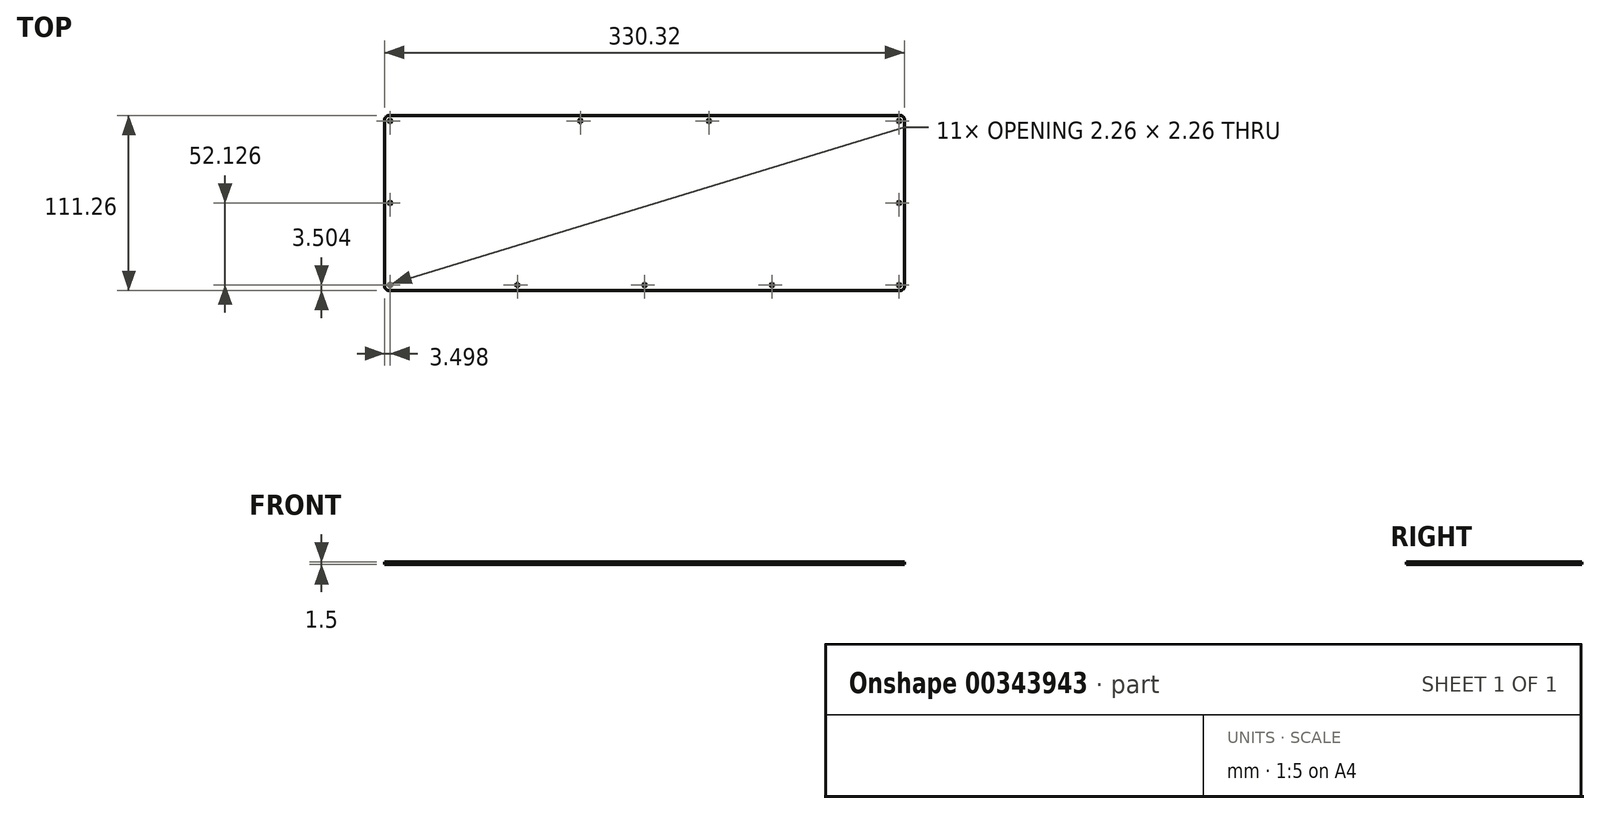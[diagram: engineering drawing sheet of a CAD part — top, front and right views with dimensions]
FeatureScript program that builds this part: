
annotation { "Feature Type Name" : "Feature", "Feature Type Description" : "" }
export const myFeature = defineFeature(function(context is Context, id is Id, definition is map)
    precondition{}
    {
        {
            var Q0;
            Q0=qCreatedBy(makeId("Top.planeOp"),FACE);
            var sketch = newSketch(context, id + "F0", { "sketchPlane" : qUnion([Q0])});
            skLineSegment(sketch, "E0", {"start": v(162.16, 55.62) * mm, "end": v(162.4, 55.62) * mm});
            skLineSegment(sketch, "E1", {"start": v(162.4, 55.62) * mm, "end": v(162.63, 55.59) * mm});
            skLineSegment(sketch, "E2", {"start": v(162.63, 55.59) * mm, "end": v(162.86, 55.54) * mm});
            skLineSegment(sketch, "E3", {"start": v(162.86, 55.54) * mm, "end": v(163.1, 55.48) * mm});
            skLineSegment(sketch, "E4", {"start": v(163.1, 55.48) * mm, "end": v(163.31, 55.4) * mm});
            skLineSegment(sketch, "E5", {"start": v(163.31, 55.4) * mm, "end": v(163.53, 55.3) * mm});
            skLineSegment(sketch, "E6", {"start": v(163.53, 55.3) * mm, "end": v(163.73, 55.18) * mm});
            skLineSegment(sketch, "E7", {"start": v(163.73, 55.18) * mm, "end": v(163.93, 55.05) * mm});
            skLineSegment(sketch, "E8", {"start": v(163.93, 55.05) * mm, "end": v(164.11, 54.9) * mm});
            skLineSegment(sketch, "E9", {"start": v(164.11, 54.9) * mm, "end": v(164.29, 54.75) * mm});
            skLineSegment(sketch, "E10", {"start": v(164.29, 54.75) * mm, "end": v(164.45, 54.57) * mm});
            skLineSegment(sketch, "E11", {"start": v(164.45, 54.57) * mm, "end": v(164.6, 54.39) * mm});
            skLineSegment(sketch, "E12", {"start": v(164.6, 54.39) * mm, "end": v(164.72, 54.2) * mm});
            skLineSegment(sketch, "E13", {"start": v(164.72, 54.2) * mm, "end": v(164.84, 53.99) * mm});
            skLineSegment(sketch, "E14", {"start": v(164.84, 53.99) * mm, "end": v(164.93, 53.77) * mm});
            skLineSegment(sketch, "E15", {"start": v(164.93, 53.77) * mm, "end": v(165.02, 53.55) * mm});
            skLineSegment(sketch, "E16", {"start": v(165.02, 53.55) * mm, "end": v(165.08, 53.33) * mm});
            skLineSegment(sketch, "E17", {"start": v(165.08, 53.33) * mm, "end": v(165.13, 53.1) * mm});
            skLineSegment(sketch, "E18", {"start": v(165.13, 53.1) * mm, "end": v(165.15, 52.86) * mm});
            skLineSegment(sketch, "E19", {"start": v(165.15, 52.86) * mm, "end": v(165.16, 52.62) * mm});
            skLineSegment(sketch, "E20", {"start": v(165.16, 52.62) * mm, "end": v(165.16, -52.63) * mm});
            skLineSegment(sketch, "E21", {"start": v(165.16, -52.63) * mm, "end": v(165.15, -52.86) * mm});
            skLineSegment(sketch, "E22", {"start": v(165.15, -52.86) * mm, "end": v(165.13, -53.1) * mm});
            skLineSegment(sketch, "E23", {"start": v(165.13, -53.1) * mm, "end": v(165.08, -53.33) * mm});
            skLineSegment(sketch, "E24", {"start": v(165.08, -53.33) * mm, "end": v(165.02, -53.55) * mm});
            skLineSegment(sketch, "E25", {"start": v(165.02, -53.55) * mm, "end": v(164.93, -53.77) * mm});
            skLineSegment(sketch, "E26", {"start": v(164.93, -53.77) * mm, "end": v(164.84, -53.99) * mm});
            skLineSegment(sketch, "E27", {"start": v(164.84, -53.99) * mm, "end": v(164.72, -54.2) * mm});
            skLineSegment(sketch, "E28", {"start": v(164.72, -54.2) * mm, "end": v(164.6, -54.39) * mm});
            skLineSegment(sketch, "E29", {"start": v(164.6, -54.39) * mm, "end": v(164.45, -54.57) * mm});
            skLineSegment(sketch, "E30", {"start": v(164.45, -54.57) * mm, "end": v(164.29, -54.75) * mm});
            skLineSegment(sketch, "E31", {"start": v(164.29, -54.75) * mm, "end": v(164.11, -54.9) * mm});
            skLineSegment(sketch, "E32", {"start": v(164.11, -54.9) * mm, "end": v(163.93, -55.05) * mm});
            skLineSegment(sketch, "E33", {"start": v(163.93, -55.05) * mm, "end": v(163.73, -55.18) * mm});
            skLineSegment(sketch, "E34", {"start": v(163.73, -55.18) * mm, "end": v(163.53, -55.3) * mm});
            skLineSegment(sketch, "E35", {"start": v(163.53, -55.3) * mm, "end": v(163.31, -55.4) * mm});
            skLineSegment(sketch, "E36", {"start": v(163.31, -55.4) * mm, "end": v(163.1, -55.48) * mm});
            skLineSegment(sketch, "E37", {"start": v(163.1, -55.48) * mm, "end": v(162.86, -55.54) * mm});
            skLineSegment(sketch, "E38", {"start": v(162.86, -55.54) * mm, "end": v(162.63, -55.59) * mm});
            skLineSegment(sketch, "E39", {"start": v(162.63, -55.59) * mm, "end": v(162.4, -55.62) * mm});
            skLineSegment(sketch, "E40", {"start": v(162.4, -55.62) * mm, "end": v(162.16, -55.63) * mm});
            skLineSegment(sketch, "E41", {"start": v(162.16, -55.63) * mm, "end": v(-162.16, -55.63) * mm});
            skLineSegment(sketch, "E42", {"start": v(-162.16, -55.63) * mm, "end": v(-162.4, -55.62) * mm});
            skLineSegment(sketch, "E43", {"start": v(-162.4, -55.62) * mm, "end": v(-162.63, -55.59) * mm});
            skLineSegment(sketch, "E44", {"start": v(-162.63, -55.59) * mm, "end": v(-162.86, -55.54) * mm});
            skLineSegment(sketch, "E45", {"start": v(-162.86, -55.54) * mm, "end": v(-163.09, -55.48) * mm});
            skLineSegment(sketch, "E46", {"start": v(-163.09, -55.48) * mm, "end": v(-163.31, -55.4) * mm});
            skLineSegment(sketch, "E47", {"start": v(-163.31, -55.4) * mm, "end": v(-163.52, -55.3) * mm});
            skLineSegment(sketch, "E48", {"start": v(-163.52, -55.3) * mm, "end": v(-163.73, -55.18) * mm});
            skLineSegment(sketch, "E49", {"start": v(-163.73, -55.18) * mm, "end": v(-163.93, -55.05) * mm});
            skLineSegment(sketch, "E50", {"start": v(-163.93, -55.05) * mm, "end": v(-164.11, -54.9) * mm});
            skLineSegment(sketch, "E51", {"start": v(-164.11, -54.9) * mm, "end": v(-164.28, -54.75) * mm});
            skLineSegment(sketch, "E52", {"start": v(-164.28, -54.75) * mm, "end": v(-164.44, -54.57) * mm});
            skLineSegment(sketch, "E53", {"start": v(-164.44, -54.57) * mm, "end": v(-164.6, -54.39) * mm});
            skLineSegment(sketch, "E54", {"start": v(-164.6, -54.39) * mm, "end": v(-164.72, -54.2) * mm});
            skLineSegment(sketch, "E55", {"start": v(-164.72, -54.2) * mm, "end": v(-164.84, -53.99) * mm});
            skLineSegment(sketch, "E56", {"start": v(-164.84, -53.99) * mm, "end": v(-164.93, -53.77) * mm});
            skLineSegment(sketch, "E57", {"start": v(-164.93, -53.77) * mm, "end": v(-165.02, -53.55) * mm});
            skLineSegment(sketch, "E58", {"start": v(-165.02, -53.55) * mm, "end": v(-165.08, -53.33) * mm});
            skLineSegment(sketch, "E59", {"start": v(-165.08, -53.33) * mm, "end": v(-165.13, -53.1) * mm});
            skLineSegment(sketch, "E60", {"start": v(-165.13, -53.1) * mm, "end": v(-165.15, -52.86) * mm});
            skLineSegment(sketch, "E61", {"start": v(-165.15, -52.86) * mm, "end": v(-165.16, -52.63) * mm});
            skLineSegment(sketch, "E62", {"start": v(-165.16, -52.63) * mm, "end": v(-165.16, 52.62) * mm});
            skLineSegment(sketch, "E63", {"start": v(-165.16, 52.62) * mm, "end": v(-165.15, 52.86) * mm});
            skLineSegment(sketch, "E64", {"start": v(-165.15, 52.86) * mm, "end": v(-165.13, 53.1) * mm});
            skLineSegment(sketch, "E65", {"start": v(-165.13, 53.1) * mm, "end": v(-165.08, 53.33) * mm});
            skLineSegment(sketch, "E66", {"start": v(-165.08, 53.33) * mm, "end": v(-165.02, 53.55) * mm});
            skLineSegment(sketch, "E67", {"start": v(-165.02, 53.55) * mm, "end": v(-164.93, 53.77) * mm});
            skLineSegment(sketch, "E68", {"start": v(-164.93, 53.77) * mm, "end": v(-164.84, 53.99) * mm});
            skLineSegment(sketch, "E69", {"start": v(-164.84, 53.99) * mm, "end": v(-164.72, 54.2) * mm});
            skLineSegment(sketch, "E70", {"start": v(-164.72, 54.2) * mm, "end": v(-164.6, 54.39) * mm});
            skLineSegment(sketch, "E71", {"start": v(-164.6, 54.39) * mm, "end": v(-164.44, 54.57) * mm});
            skLineSegment(sketch, "E72", {"start": v(-164.44, 54.57) * mm, "end": v(-164.28, 54.75) * mm});
            skLineSegment(sketch, "E73", {"start": v(-164.28, 54.75) * mm, "end": v(-164.11, 54.9) * mm});
            skLineSegment(sketch, "E74", {"start": v(-164.11, 54.9) * mm, "end": v(-163.93, 55.05) * mm});
            skLineSegment(sketch, "E75", {"start": v(-163.93, 55.05) * mm, "end": v(-163.73, 55.18) * mm});
            skLineSegment(sketch, "E76", {"start": v(-163.73, 55.18) * mm, "end": v(-163.52, 55.3) * mm});
            skLineSegment(sketch, "E77", {"start": v(-163.52, 55.3) * mm, "end": v(-163.31, 55.4) * mm});
            skLineSegment(sketch, "E78", {"start": v(-163.31, 55.4) * mm, "end": v(-163.09, 55.48) * mm});
            skLineSegment(sketch, "E79", {"start": v(-163.09, 55.48) * mm, "end": v(-162.86, 55.54) * mm});
            skLineSegment(sketch, "E80", {"start": v(-162.86, 55.54) * mm, "end": v(-162.63, 55.59) * mm});
            skLineSegment(sketch, "E81", {"start": v(-162.63, 55.59) * mm, "end": v(-162.4, 55.62) * mm});
            skLineSegment(sketch, "E82", {"start": v(-162.4, 55.62) * mm, "end": v(-162.16, 55.63) * mm});
            skLineSegment(sketch, "E83", {"start": v(-162.16, 55.63) * mm, "end": v(162.16, 55.62) * mm});
            skLineSegment(sketch, "E84", {"start": v(161.31, -51.05) * mm, "end": v(161, -51.21) * mm});
            skLineSegment(sketch, "E85", {"start": v(161, -51.21) * mm, "end": v(160.75, -51.46) * mm});
            skLineSegment(sketch, "E86", {"start": v(160.75, -51.46) * mm, "end": v(160.59, -51.78) * mm});
            skLineSegment(sketch, "E87", {"start": v(160.59, -51.78) * mm, "end": v(160.53, -52.13) * mm});
            skLineSegment(sketch, "E88", {"start": v(160.53, -52.13) * mm, "end": v(160.59, -52.48) * mm});
            skLineSegment(sketch, "E89", {"start": v(160.59, -52.48) * mm, "end": v(160.75, -52.79) * mm});
            skLineSegment(sketch, "E90", {"start": v(160.75, -52.79) * mm, "end": v(161, -53.04) * mm});
            skLineSegment(sketch, "E91", {"start": v(161, -53.04) * mm, "end": v(161.31, -53.2) * mm});
            skLineSegment(sketch, "E92", {"start": v(161.31, -53.2) * mm, "end": v(161.66, -53.26) * mm});
            skLineSegment(sketch, "E93", {"start": v(161.66, -53.26) * mm, "end": v(162.01, -53.2) * mm});
            skLineSegment(sketch, "E94", {"start": v(162.01, -53.2) * mm, "end": v(162.33, -53.04) * mm});
            skLineSegment(sketch, "E95", {"start": v(162.33, -53.04) * mm, "end": v(162.58, -52.79) * mm});
            skLineSegment(sketch, "E96", {"start": v(162.58, -52.79) * mm, "end": v(162.74, -52.48) * mm});
            skLineSegment(sketch, "E97", {"start": v(162.74, -52.48) * mm, "end": v(162.8, -52.13) * mm});
            skLineSegment(sketch, "E98", {"start": v(162.8, -52.13) * mm, "end": v(162.74, -51.78) * mm});
            skLineSegment(sketch, "E99", {"start": v(162.74, -51.78) * mm, "end": v(162.58, -51.46) * mm});
            skLineSegment(sketch, "E100", {"start": v(162.58, -51.46) * mm, "end": v(162.33, -51.21) * mm});
            skLineSegment(sketch, "E101", {"start": v(162.33, -51.21) * mm, "end": v(162.01, -51.05) * mm});
            skLineSegment(sketch, "E102", {"start": v(162.01, -51.05) * mm, "end": v(161.66, -51) * mm});
            skLineSegment(sketch, "E103", {"start": v(161.66, -51) * mm, "end": v(161.31, -51.05) * mm});
            skLineSegment(sketch, "E104", {"start": v(80.48, -51.05) * mm, "end": v(80.17, -51.21) * mm});
            skLineSegment(sketch, "E105", {"start": v(80.17, -51.21) * mm, "end": v(79.92, -51.46) * mm});
            skLineSegment(sketch, "E106", {"start": v(79.92, -51.46) * mm, "end": v(79.76, -51.78) * mm});
            skLineSegment(sketch, "E107", {"start": v(79.76, -51.78) * mm, "end": v(79.7, -52.13) * mm});
            skLineSegment(sketch, "E108", {"start": v(79.7, -52.13) * mm, "end": v(79.76, -52.48) * mm});
            skLineSegment(sketch, "E109", {"start": v(79.76, -52.48) * mm, "end": v(79.92, -52.79) * mm});
            skLineSegment(sketch, "E110", {"start": v(79.92, -52.79) * mm, "end": v(80.17, -53.04) * mm});
            skLineSegment(sketch, "E111", {"start": v(80.17, -53.04) * mm, "end": v(80.48, -53.2) * mm});
            skLineSegment(sketch, "E112", {"start": v(80.48, -53.2) * mm, "end": v(80.83, -53.26) * mm});
            skLineSegment(sketch, "E113", {"start": v(80.83, -53.26) * mm, "end": v(81.18, -53.2) * mm});
            skLineSegment(sketch, "E114", {"start": v(81.18, -53.2) * mm, "end": v(81.5, -53.04) * mm});
            skLineSegment(sketch, "E115", {"start": v(81.5, -53.04) * mm, "end": v(81.75, -52.79) * mm});
            skLineSegment(sketch, "E116", {"start": v(81.75, -52.79) * mm, "end": v(81.9, -52.48) * mm});
            skLineSegment(sketch, "E117", {"start": v(81.9, -52.48) * mm, "end": v(81.96, -52.13) * mm});
            skLineSegment(sketch, "E118", {"start": v(81.96, -52.13) * mm, "end": v(81.9, -51.78) * mm});
            skLineSegment(sketch, "E119", {"start": v(81.9, -51.78) * mm, "end": v(81.75, -51.46) * mm});
            skLineSegment(sketch, "E120", {"start": v(81.75, -51.46) * mm, "end": v(81.5, -51.21) * mm});
            skLineSegment(sketch, "E121", {"start": v(81.5, -51.21) * mm, "end": v(81.18, -51.05) * mm});
            skLineSegment(sketch, "E122", {"start": v(81.18, -51.05) * mm, "end": v(80.83, -51) * mm});
            skLineSegment(sketch, "E123", {"start": v(80.83, -51) * mm, "end": v(80.48, -51.05) * mm});
            skLineSegment(sketch, "E124", {"start": v(-0.35, -51.05) * mm, "end": v(-0.66, -51.21) * mm});
            skLineSegment(sketch, "E125", {"start": v(-0.66, -51.21) * mm, "end": v(-0.91, -51.46) * mm});
            skLineSegment(sketch, "E126", {"start": v(-0.91, -51.46) * mm, "end": v(-1.07, -51.78) * mm});
            skLineSegment(sketch, "E127", {"start": v(-1.07, -51.78) * mm, "end": v(-1.13, -52.13) * mm});
            skLineSegment(sketch, "E128", {"start": v(-1.13, -52.13) * mm, "end": v(-1.07, -52.48) * mm});
            skLineSegment(sketch, "E129", {"start": v(-1.07, -52.48) * mm, "end": v(-0.91, -52.79) * mm});
            skLineSegment(sketch, "E130", {"start": v(-0.91, -52.79) * mm, "end": v(-0.66, -53.04) * mm});
            skLineSegment(sketch, "E131", {"start": v(-0.66, -53.04) * mm, "end": v(-0.35, -53.2) * mm});
            skLineSegment(sketch, "E132", {"start": v(-0.35, -53.2) * mm, "end": v(0, -53.26) * mm});
            skLineSegment(sketch, "E133", {"start": v(0, -53.26) * mm, "end": v(0.35, -53.2) * mm});
            skLineSegment(sketch, "E134", {"start": v(0.35, -53.2) * mm, "end": v(0.67, -53.04) * mm});
            skLineSegment(sketch, "E135", {"start": v(0.67, -53.04) * mm, "end": v(0.92, -52.79) * mm});
            skLineSegment(sketch, "E136", {"start": v(0.92, -52.79) * mm, "end": v(1.07, -52.48) * mm});
            skLineSegment(sketch, "E137", {"start": v(1.07, -52.48) * mm, "end": v(1.13, -52.13) * mm});
            skLineSegment(sketch, "E138", {"start": v(1.13, -52.13) * mm, "end": v(1.07, -51.78) * mm});
            skLineSegment(sketch, "E139", {"start": v(1.07, -51.78) * mm, "end": v(0.92, -51.46) * mm});
            skLineSegment(sketch, "E140", {"start": v(0.92, -51.46) * mm, "end": v(0.67, -51.21) * mm});
            skLineSegment(sketch, "E141", {"start": v(0.67, -51.21) * mm, "end": v(0.35, -51.05) * mm});
            skLineSegment(sketch, "E142", {"start": v(0.35, -51.05) * mm, "end": v(0, -51) * mm});
            skLineSegment(sketch, "E143", {"start": v(0, -51) * mm, "end": v(-0.35, -51.05) * mm});
            skLineSegment(sketch, "E144", {"start": v(-81.18, -51.05) * mm, "end": v(-81.5, -51.21) * mm});
            skLineSegment(sketch, "E145", {"start": v(-81.5, -51.21) * mm, "end": v(-81.75, -51.46) * mm});
            skLineSegment(sketch, "E146", {"start": v(-81.75, -51.46) * mm, "end": v(-81.9, -51.78) * mm});
            skLineSegment(sketch, "E147", {"start": v(-81.9, -51.78) * mm, "end": v(-81.96, -52.13) * mm});
            skLineSegment(sketch, "E148", {"start": v(-81.96, -52.13) * mm, "end": v(-81.9, -52.48) * mm});
            skLineSegment(sketch, "E149", {"start": v(-81.9, -52.48) * mm, "end": v(-81.75, -52.79) * mm});
            skLineSegment(sketch, "E150", {"start": v(-81.75, -52.79) * mm, "end": v(-81.5, -53.04) * mm});
            skLineSegment(sketch, "E151", {"start": v(-81.5, -53.04) * mm, "end": v(-81.18, -53.2) * mm});
            skLineSegment(sketch, "E152", {"start": v(-81.18, -53.2) * mm, "end": v(-80.83, -53.26) * mm});
            skLineSegment(sketch, "E153", {"start": v(-80.83, -53.26) * mm, "end": v(-80.48, -53.2) * mm});
            skLineSegment(sketch, "E154", {"start": v(-80.48, -53.2) * mm, "end": v(-80.17, -53.04) * mm});
            skLineSegment(sketch, "E155", {"start": v(-80.17, -53.04) * mm, "end": v(-79.92, -52.79) * mm});
            skLineSegment(sketch, "E156", {"start": v(-79.92, -52.79) * mm, "end": v(-79.76, -52.48) * mm});
            skLineSegment(sketch, "E157", {"start": v(-79.76, -52.48) * mm, "end": v(-79.7, -52.13) * mm});
            skLineSegment(sketch, "E158", {"start": v(-79.7, -52.13) * mm, "end": v(-79.76, -51.78) * mm});
            skLineSegment(sketch, "E159", {"start": v(-79.76, -51.78) * mm, "end": v(-79.92, -51.46) * mm});
            skLineSegment(sketch, "E160", {"start": v(-79.92, -51.46) * mm, "end": v(-80.17, -51.21) * mm});
            skLineSegment(sketch, "E161", {"start": v(-80.17, -51.21) * mm, "end": v(-80.48, -51.05) * mm});
            skLineSegment(sketch, "E162", {"start": v(-80.48, -51.05) * mm, "end": v(-80.83, -51) * mm});
            skLineSegment(sketch, "E163", {"start": v(-80.83, -51) * mm, "end": v(-81.18, -51.05) * mm});
            skLineSegment(sketch, "E164", {"start": v(-162.01, -51.05) * mm, "end": v(-162.33, -51.21) * mm});
            skLineSegment(sketch, "E165", {"start": v(-162.33, -51.21) * mm, "end": v(-162.58, -51.46) * mm});
            skLineSegment(sketch, "E166", {"start": v(-162.58, -51.46) * mm, "end": v(-162.74, -51.78) * mm});
            skLineSegment(sketch, "E167", {"start": v(-162.74, -51.78) * mm, "end": v(-162.8, -52.13) * mm});
            skLineSegment(sketch, "E168", {"start": v(-162.8, -52.13) * mm, "end": v(-162.74, -52.48) * mm});
            skLineSegment(sketch, "E169", {"start": v(-162.74, -52.48) * mm, "end": v(-162.58, -52.79) * mm});
            skLineSegment(sketch, "E170", {"start": v(-162.58, -52.79) * mm, "end": v(-162.33, -53.04) * mm});
            skLineSegment(sketch, "E171", {"start": v(-162.33, -53.04) * mm, "end": v(-162.01, -53.2) * mm});
            skLineSegment(sketch, "E172", {"start": v(-162.01, -53.2) * mm, "end": v(-161.66, -53.26) * mm});
            skLineSegment(sketch, "E173", {"start": v(-161.66, -53.26) * mm, "end": v(-161.31, -53.2) * mm});
            skLineSegment(sketch, "E174", {"start": v(-161.31, -53.2) * mm, "end": v(-161, -53.04) * mm});
            skLineSegment(sketch, "E175", {"start": v(-161, -53.04) * mm, "end": v(-160.75, -52.79) * mm});
            skLineSegment(sketch, "E176", {"start": v(-160.75, -52.79) * mm, "end": v(-160.59, -52.48) * mm});
            skLineSegment(sketch, "E177", {"start": v(-160.59, -52.48) * mm, "end": v(-160.53, -52.13) * mm});
            skLineSegment(sketch, "E178", {"start": v(-160.53, -52.13) * mm, "end": v(-160.59, -51.78) * mm});
            skLineSegment(sketch, "E179", {"start": v(-160.59, -51.78) * mm, "end": v(-160.75, -51.46) * mm});
            skLineSegment(sketch, "E180", {"start": v(-160.75, -51.46) * mm, "end": v(-161, -51.21) * mm});
            skLineSegment(sketch, "E181", {"start": v(-161, -51.21) * mm, "end": v(-161.31, -51.05) * mm});
            skLineSegment(sketch, "E182", {"start": v(-161.31, -51.05) * mm, "end": v(-161.66, -51) * mm});
            skLineSegment(sketch, "E183", {"start": v(-161.66, -51) * mm, "end": v(-162.01, -51.05) * mm});
            skLineSegment(sketch, "E184", {"start": v(161.31, 1.08) * mm, "end": v(161, 0.91) * mm});
            skLineSegment(sketch, "E185", {"start": v(161, 0.91) * mm, "end": v(160.75, 0.66) * mm});
            skLineSegment(sketch, "E186", {"start": v(160.75, 0.66) * mm, "end": v(160.59, 0.35) * mm});
            skLineSegment(sketch, "E187", {"start": v(160.59, 0.35) * mm, "end": v(160.53, 0) * mm});
            skLineSegment(sketch, "E188", {"start": v(160.53, 0) * mm, "end": v(160.59, -0.35) * mm});
            skLineSegment(sketch, "E189", {"start": v(160.59, -0.35) * mm, "end": v(160.75, -0.66) * mm});
            skLineSegment(sketch, "E190", {"start": v(160.75, -0.66) * mm, "end": v(161, -0.91) * mm});
            skLineSegment(sketch, "E191", {"start": v(161, -0.91) * mm, "end": v(161.31, -1.07) * mm});
            skLineSegment(sketch, "E192", {"start": v(161.31, -1.07) * mm, "end": v(161.66, -1.13) * mm});
            skLineSegment(sketch, "E193", {"start": v(161.66, -1.13) * mm, "end": v(162.01, -1.07) * mm});
            skLineSegment(sketch, "E194", {"start": v(162.01, -1.07) * mm, "end": v(162.33, -0.91) * mm});
            skLineSegment(sketch, "E195", {"start": v(162.33, -0.91) * mm, "end": v(162.58, -0.66) * mm});
            skLineSegment(sketch, "E196", {"start": v(162.58, -0.66) * mm, "end": v(162.74, -0.35) * mm});
            skLineSegment(sketch, "E197", {"start": v(162.74, -0.35) * mm, "end": v(162.8, 0) * mm});
            skLineSegment(sketch, "E198", {"start": v(162.8, 0) * mm, "end": v(162.74, 0.35) * mm});
            skLineSegment(sketch, "E199", {"start": v(162.74, 0.35) * mm, "end": v(162.58, 0.66) * mm});
            skLineSegment(sketch, "E200", {"start": v(162.58, 0.66) * mm, "end": v(162.33, 0.91) * mm});
            skLineSegment(sketch, "E201", {"start": v(162.33, 0.91) * mm, "end": v(162.01, 1.08) * mm});
            skLineSegment(sketch, "E202", {"start": v(162.01, 1.08) * mm, "end": v(161.66, 1.13) * mm});
            skLineSegment(sketch, "E203", {"start": v(161.66, 1.13) * mm, "end": v(161.31, 1.08) * mm});
            skLineSegment(sketch, "E204", {"start": v(-162.01, 1.08) * mm, "end": v(-162.33, 0.91) * mm});
            skLineSegment(sketch, "E205", {"start": v(-162.33, 0.91) * mm, "end": v(-162.58, 0.66) * mm});
            skLineSegment(sketch, "E206", {"start": v(-162.58, 0.66) * mm, "end": v(-162.74, 0.35) * mm});
            skLineSegment(sketch, "E207", {"start": v(-162.74, 0.35) * mm, "end": v(-162.8, 0) * mm});
            skLineSegment(sketch, "E208", {"start": v(-162.8, 0) * mm, "end": v(-162.74, -0.35) * mm});
            skLineSegment(sketch, "E209", {"start": v(-162.74, -0.35) * mm, "end": v(-162.58, -0.66) * mm});
            skLineSegment(sketch, "E210", {"start": v(-162.58, -0.66) * mm, "end": v(-162.33, -0.91) * mm});
            skLineSegment(sketch, "E211", {"start": v(-162.33, -0.91) * mm, "end": v(-162.01, -1.07) * mm});
            skLineSegment(sketch, "E212", {"start": v(-162.01, -1.07) * mm, "end": v(-161.66, -1.13) * mm});
            skLineSegment(sketch, "E213", {"start": v(-161.66, -1.13) * mm, "end": v(-161.31, -1.07) * mm});
            skLineSegment(sketch, "E214", {"start": v(-161.31, -1.07) * mm, "end": v(-161, -0.91) * mm});
            skLineSegment(sketch, "E215", {"start": v(-161, -0.91) * mm, "end": v(-160.75, -0.66) * mm});
            skLineSegment(sketch, "E216", {"start": v(-160.75, -0.66) * mm, "end": v(-160.59, -0.35) * mm});
            skLineSegment(sketch, "E217", {"start": v(-160.59, -0.35) * mm, "end": v(-160.53, 0) * mm});
            skLineSegment(sketch, "E218", {"start": v(-160.53, 0) * mm, "end": v(-160.59, 0.35) * mm});
            skLineSegment(sketch, "E219", {"start": v(-160.59, 0.35) * mm, "end": v(-160.75, 0.66) * mm});
            skLineSegment(sketch, "E220", {"start": v(-160.75, 0.66) * mm, "end": v(-161, 0.91) * mm});
            skLineSegment(sketch, "E221", {"start": v(-161, 0.91) * mm, "end": v(-161.31, 1.08) * mm});
            skLineSegment(sketch, "E222", {"start": v(-161.31, 1.08) * mm, "end": v(-161.66, 1.13) * mm});
            skLineSegment(sketch, "E223", {"start": v(-161.66, 1.13) * mm, "end": v(-162.01, 1.08) * mm});
            skLineSegment(sketch, "E224", {"start": v(-41.18, 53.2) * mm, "end": v(-41.5, 53.04) * mm});
            skLineSegment(sketch, "E225", {"start": v(-41.5, 53.04) * mm, "end": v(-41.75, 52.8) * mm});
            skLineSegment(sketch, "E226", {"start": v(-41.75, 52.8) * mm, "end": v(-41.9, 52.47) * mm});
            skLineSegment(sketch, "E227", {"start": v(-41.9, 52.47) * mm, "end": v(-41.96, 52.12) * mm});
            skLineSegment(sketch, "E228", {"start": v(-41.96, 52.12) * mm, "end": v(-41.9, 51.78) * mm});
            skLineSegment(sketch, "E229", {"start": v(-41.9, 51.78) * mm, "end": v(-41.75, 51.46) * mm});
            skLineSegment(sketch, "E230", {"start": v(-41.75, 51.46) * mm, "end": v(-41.5, 51.21) * mm});
            skLineSegment(sketch, "E231", {"start": v(-41.5, 51.21) * mm, "end": v(-41.18, 51.05) * mm});
            skLineSegment(sketch, "E232", {"start": v(-41.18, 51.05) * mm, "end": v(-40.83, 51) * mm});
            skLineSegment(sketch, "E233", {"start": v(-40.83, 51) * mm, "end": v(-40.48, 51.05) * mm});
            skLineSegment(sketch, "E234", {"start": v(-40.48, 51.05) * mm, "end": v(-40.17, 51.21) * mm});
            skLineSegment(sketch, "E235", {"start": v(-40.17, 51.21) * mm, "end": v(-39.92, 51.46) * mm});
            skLineSegment(sketch, "E236", {"start": v(-39.92, 51.46) * mm, "end": v(-39.76, 51.78) * mm});
            skLineSegment(sketch, "E237", {"start": v(-39.76, 51.78) * mm, "end": v(-39.7, 52.12) * mm});
            skLineSegment(sketch, "E238", {"start": v(-39.7, 52.12) * mm, "end": v(-39.76, 52.47) * mm});
            skLineSegment(sketch, "E239", {"start": v(-39.76, 52.47) * mm, "end": v(-39.92, 52.8) * mm});
            skLineSegment(sketch, "E240", {"start": v(-39.92, 52.8) * mm, "end": v(-40.17, 53.04) * mm});
            skLineSegment(sketch, "E241", {"start": v(-40.17, 53.04) * mm, "end": v(-40.48, 53.2) * mm});
            skLineSegment(sketch, "E242", {"start": v(-40.48, 53.2) * mm, "end": v(-40.83, 53.26) * mm});
            skLineSegment(sketch, "E243", {"start": v(-40.83, 53.26) * mm, "end": v(-41.18, 53.2) * mm});
            skLineSegment(sketch, "E244", {"start": v(40.48, 53.2) * mm, "end": v(40.17, 53.04) * mm});
            skLineSegment(sketch, "E245", {"start": v(40.17, 53.04) * mm, "end": v(39.92, 52.8) * mm});
            skLineSegment(sketch, "E246", {"start": v(39.92, 52.8) * mm, "end": v(39.76, 52.47) * mm});
            skLineSegment(sketch, "E247", {"start": v(39.76, 52.47) * mm, "end": v(39.7, 52.12) * mm});
            skLineSegment(sketch, "E248", {"start": v(39.7, 52.12) * mm, "end": v(39.76, 51.78) * mm});
            skLineSegment(sketch, "E249", {"start": v(39.76, 51.78) * mm, "end": v(39.92, 51.46) * mm});
            skLineSegment(sketch, "E250", {"start": v(39.92, 51.46) * mm, "end": v(40.17, 51.21) * mm});
            skLineSegment(sketch, "E251", {"start": v(40.17, 51.21) * mm, "end": v(40.48, 51.05) * mm});
            skLineSegment(sketch, "E252", {"start": v(40.48, 51.05) * mm, "end": v(40.83, 51) * mm});
            skLineSegment(sketch, "E253", {"start": v(40.83, 51) * mm, "end": v(41.18, 51.05) * mm});
            skLineSegment(sketch, "E254", {"start": v(41.18, 51.05) * mm, "end": v(41.5, 51.21) * mm});
            skLineSegment(sketch, "E255", {"start": v(41.5, 51.21) * mm, "end": v(41.75, 51.46) * mm});
            skLineSegment(sketch, "E256", {"start": v(41.75, 51.46) * mm, "end": v(41.9, 51.78) * mm});
            skLineSegment(sketch, "E257", {"start": v(41.9, 51.78) * mm, "end": v(41.96, 52.12) * mm});
            skLineSegment(sketch, "E258", {"start": v(41.96, 52.12) * mm, "end": v(41.9, 52.47) * mm});
            skLineSegment(sketch, "E259", {"start": v(41.9, 52.47) * mm, "end": v(41.75, 52.8) * mm});
            skLineSegment(sketch, "E260", {"start": v(41.75, 52.8) * mm, "end": v(41.5, 53.04) * mm});
            skLineSegment(sketch, "E261", {"start": v(41.5, 53.04) * mm, "end": v(41.18, 53.2) * mm});
            skLineSegment(sketch, "E262", {"start": v(41.18, 53.2) * mm, "end": v(40.83, 53.26) * mm});
            skLineSegment(sketch, "E263", {"start": v(40.83, 53.26) * mm, "end": v(40.48, 53.2) * mm});
            skLineSegment(sketch, "E264", {"start": v(161.31, 53.2) * mm, "end": v(161, 53.04) * mm});
            skLineSegment(sketch, "E265", {"start": v(161, 53.04) * mm, "end": v(160.75, 52.8) * mm});
            skLineSegment(sketch, "E266", {"start": v(160.75, 52.8) * mm, "end": v(160.59, 52.47) * mm});
            skLineSegment(sketch, "E267", {"start": v(160.59, 52.47) * mm, "end": v(160.53, 52.12) * mm});
            skLineSegment(sketch, "E268", {"start": v(160.53, 52.12) * mm, "end": v(160.59, 51.78) * mm});
            skLineSegment(sketch, "E269", {"start": v(160.59, 51.78) * mm, "end": v(160.75, 51.46) * mm});
            skLineSegment(sketch, "E270", {"start": v(160.75, 51.46) * mm, "end": v(161, 51.21) * mm});
            skLineSegment(sketch, "E271", {"start": v(161, 51.21) * mm, "end": v(161.31, 51.05) * mm});
            skLineSegment(sketch, "E272", {"start": v(161.31, 51.05) * mm, "end": v(161.66, 51) * mm});
            skLineSegment(sketch, "E273", {"start": v(161.66, 51) * mm, "end": v(162.01, 51.05) * mm});
            skLineSegment(sketch, "E274", {"start": v(162.01, 51.05) * mm, "end": v(162.33, 51.21) * mm});
            skLineSegment(sketch, "E275", {"start": v(162.33, 51.21) * mm, "end": v(162.58, 51.46) * mm});
            skLineSegment(sketch, "E276", {"start": v(162.58, 51.46) * mm, "end": v(162.74, 51.78) * mm});
            skLineSegment(sketch, "E277", {"start": v(162.74, 51.78) * mm, "end": v(162.8, 52.12) * mm});
            skLineSegment(sketch, "E278", {"start": v(162.8, 52.12) * mm, "end": v(162.74, 52.47) * mm});
            skLineSegment(sketch, "E279", {"start": v(162.74, 52.47) * mm, "end": v(162.58, 52.8) * mm});
            skLineSegment(sketch, "E280", {"start": v(162.58, 52.8) * mm, "end": v(162.33, 53.04) * mm});
            skLineSegment(sketch, "E281", {"start": v(162.33, 53.04) * mm, "end": v(162.01, 53.2) * mm});
            skLineSegment(sketch, "E282", {"start": v(162.01, 53.2) * mm, "end": v(161.66, 53.26) * mm});
            skLineSegment(sketch, "E283", {"start": v(161.66, 53.26) * mm, "end": v(161.31, 53.2) * mm});
            skLineSegment(sketch, "E284", {"start": v(-162.01, 53.2) * mm, "end": v(-162.33, 53.04) * mm});
            skLineSegment(sketch, "E285", {"start": v(-162.33, 53.04) * mm, "end": v(-162.58, 52.8) * mm});
            skLineSegment(sketch, "E286", {"start": v(-162.58, 52.8) * mm, "end": v(-162.74, 52.47) * mm});
            skLineSegment(sketch, "E287", {"start": v(-162.74, 52.47) * mm, "end": v(-162.8, 52.12) * mm});
            skLineSegment(sketch, "E288", {"start": v(-162.8, 52.12) * mm, "end": v(-162.74, 51.78) * mm});
            skLineSegment(sketch, "E289", {"start": v(-162.74, 51.78) * mm, "end": v(-162.58, 51.46) * mm});
            skLineSegment(sketch, "E290", {"start": v(-162.58, 51.46) * mm, "end": v(-162.33, 51.21) * mm});
            skLineSegment(sketch, "E291", {"start": v(-162.33, 51.21) * mm, "end": v(-162.01, 51.05) * mm});
            skLineSegment(sketch, "E292", {"start": v(-162.01, 51.05) * mm, "end": v(-161.66, 51) * mm});
            skLineSegment(sketch, "E293", {"start": v(-161.66, 51) * mm, "end": v(-161.31, 51.05) * mm});
            skLineSegment(sketch, "E294", {"start": v(-161.31, 51.05) * mm, "end": v(-161, 51.21) * mm});
            skLineSegment(sketch, "E295", {"start": v(-161, 51.21) * mm, "end": v(-160.75, 51.46) * mm});
            skLineSegment(sketch, "E296", {"start": v(-160.75, 51.46) * mm, "end": v(-160.59, 51.78) * mm});
            skLineSegment(sketch, "E297", {"start": v(-160.59, 51.78) * mm, "end": v(-160.53, 52.12) * mm});
            skLineSegment(sketch, "E298", {"start": v(-160.53, 52.12) * mm, "end": v(-160.59, 52.47) * mm});
            skLineSegment(sketch, "E299", {"start": v(-160.59, 52.47) * mm, "end": v(-160.75, 52.8) * mm});
            skLineSegment(sketch, "E300", {"start": v(-160.75, 52.8) * mm, "end": v(-161, 53.04) * mm});
            skLineSegment(sketch, "E301", {"start": v(-161, 53.04) * mm, "end": v(-161.31, 53.2) * mm});
            skLineSegment(sketch, "E302", {"start": v(-161.31, 53.2) * mm, "end": v(-161.66, 53.26) * mm});
            skLineSegment(sketch, "E303", {"start": v(-161.66, 53.26) * mm, "end": v(-162.01, 53.2) * mm});
            skSolve(sketch);
        }
        {
            var Q0;
            Q0 = qSketchRegion(id + "F0", true);
            extrude(context, id + "F1", {"entities" : qUnion([Q0]), "depth" : 1.5 * mm});
        }
    });
